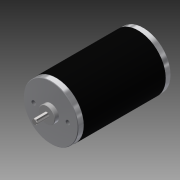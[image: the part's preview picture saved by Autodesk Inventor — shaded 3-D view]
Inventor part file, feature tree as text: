
AUTODESK INVENTOR PART (.ipt)
format: ipt  version: 2016 SP1 (Build 200210100, 210)  size: 123,904 bytes
history: native  units: in
note: dims shown in document units (in); Inventor stores cm internally (conversion verified against a paired STEP export)
features: thread x2, chamfer x1, other x1, imported_body x1
ambient origin geometry x8: Origin, YZ Plane, XZ Plane, XY Plane, X Axis, Y Axis, Z Axis, Center Point
bodies: Body1 (feature_tree)
feature tree (5):
  chamfer  "Chamfer1"  Distance=0.3937in
  other  "217-3351-STEP1"
  thread  "Thread1"  [1 undecoded]
  thread  "Thread2"  [1 undecoded]
  imported_body  "Base1"
note: 2 required parameter values undecoded (feature->parameter linkage not recoverable at this tier; creation-order binding heuristic only, values carry confidence <= 0.55)
